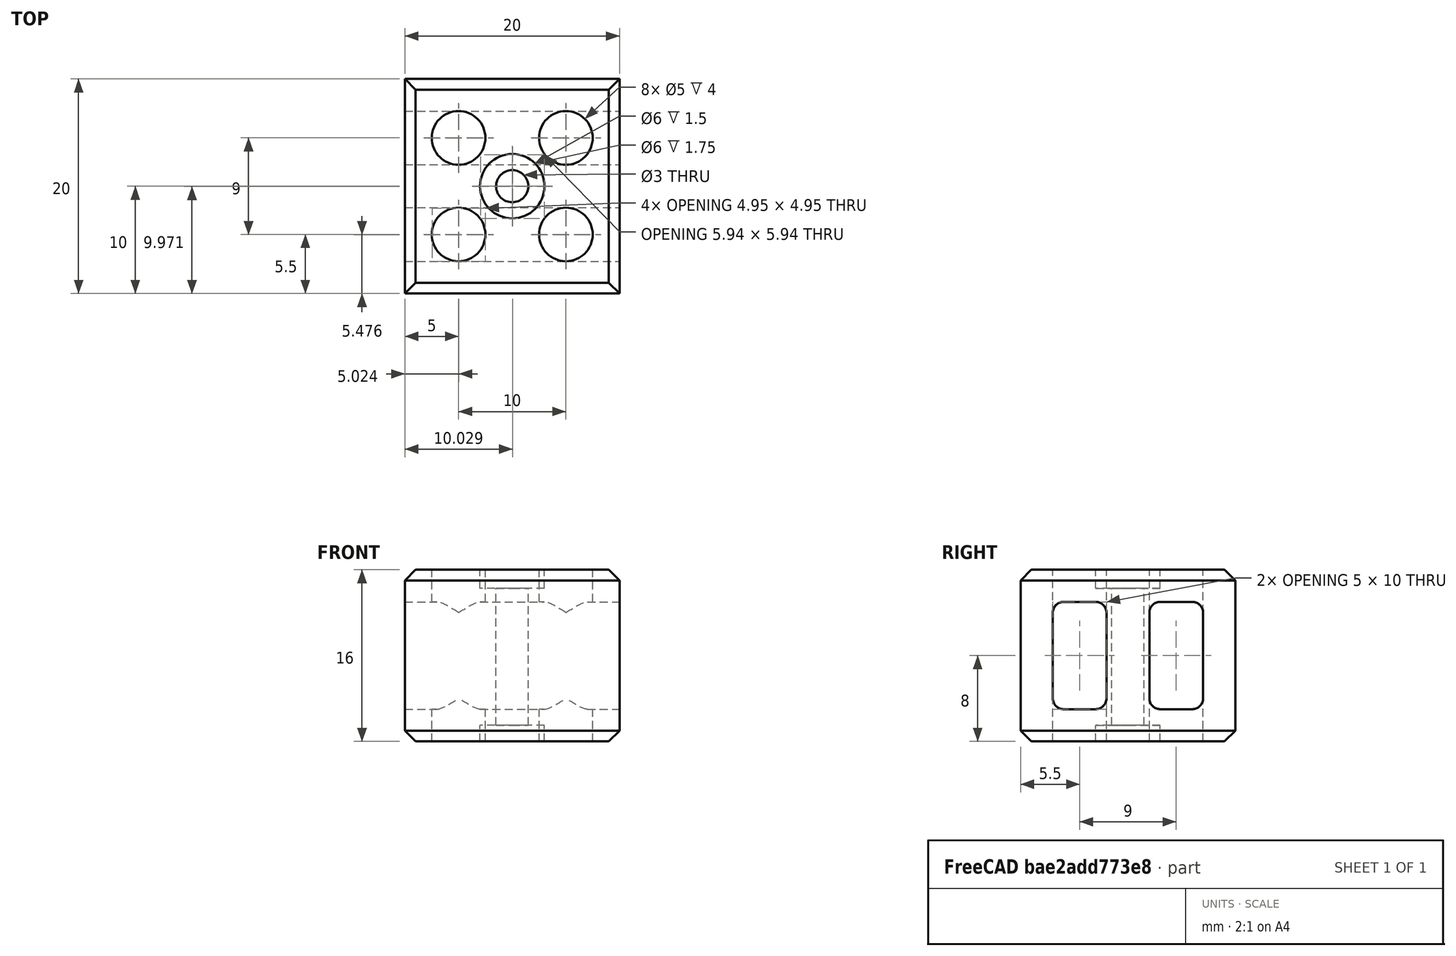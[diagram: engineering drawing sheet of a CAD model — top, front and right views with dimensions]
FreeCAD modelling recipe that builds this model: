
FCSTD DOCUMENT  (FreeCAD 0.14R3700 (Git))
Label: Cutter Ceramic Block
License: CC-BY 3.0
LicenseURL: http://creativecommons.org/licenses/by/3.0/
objects: Part::Cut×9, Part::Cylinder×7, Part::Box×3, PartDesign::Fillet×2, PartDesign::Chamfer×1
note: 22 computed .brp shape members not serialized (recipe doc carries the construction recipe); baked Part::Feature solids carry a one-line shape summary decoded from their .brp

FEATURE [Part::Box] Box  label="Cube"
  Height = 16
  Length = 20
  Width = 20
FEATURE [PartDesign::Chamfer] Chamfer
  Base = -> Box [Edge6,Edge12,Edge2,Edge10,Edge9,Edge8,Edge4,Edge11]
  Size = 1
FEATURE [Part::Box] Box001  label="Cube001"
  Height = 10
  Length = 22
  Placement = pos=(-1,12,3) rot=(0,0,1;0rad)
  Width = 5
FEATURE [Part::Box] Box002  label="Cube002"
  Height = 10
  Length = 22
  Placement = pos=(-1,3,3) rot=(0,0,1;0rad)
  Width = 5
FEATURE [Part::Cut] Cut
  Base = -> Chamfer
  Tool = -> Box002
FEATURE [Part::Cut] Cut001
  Base = -> Cut
  Tool = -> Box001
FEATURE [PartDesign::Fillet] Fillet
  Base = -> Cut001 [Edge39,Edge40,Edge38,Edge37]
  Radius = 1
FEATURE [PartDesign::Fillet] Fillet001
  Base = -> Fillet [Edge38,Edge36,Edge35,Edge33]
  Radius = 1
FEATURE [Part::Cylinder] Cylinder
  Angle = 360
  Height = 18
  Placement = pos=(5,5.5,-1) rot=(0,0,1;0rad)
  Radius = 2.5
FEATURE [Part::Cut] Cut002
  Base = -> Fillet001
  Tool = -> Cylinder
FEATURE [Part::Cylinder] Cylinder001
  Angle = 360
  Height = 18
  Placement = pos=(5,14.5,-1) rot=(0,0,1;0rad)
  Radius = 2.5
FEATURE [Part::Cylinder] Cylinder002
  Angle = 360
  Height = 18
  Placement = pos=(15,14.5,-1) rot=(0,0,1;0rad)
  Radius = 2.5
FEATURE [Part::Cylinder] Cylinder003
  Angle = 360
  Height = 18
  Placement = pos=(15,5.5,-1) rot=(0,0,1;0rad)
  Radius = 2.5
FEATURE [Part::Cut] Cut003
  Base = -> Cut002
  Tool = -> Cylinder001
FEATURE [Part::Cut] Cut004
  Base = -> Cut003
  Tool = -> Cylinder002
FEATURE [Part::Cut] Cut005
  Base = -> Cut004
  Tool = -> Cylinder003
FEATURE [Part::Cylinder] Cylinder004
  Angle = 360
  Height = 16
  Placement = pos=(10,10,0) rot=(0,0,1;0rad)
  Radius = 1.5
FEATURE [Part::Cut] Cut006
  Base = -> Cut005
  Tool = -> Cylinder004
FEATURE [Part::Cylinder] Cylinder005
  Angle = 360
  Height = 2
  Placement = pos=(10,10,-0.5) rot=(0,0,1;0rad)
  Radius = 3
FEATURE [Part::Cylinder] Cylinder006
  Angle = 360
  Height = 2
  Placement = pos=(10,10,14.25) rot=(0,0,1;0rad)
  Radius = 3
FEATURE [Part::Cut] Cut007
  Base = -> Cut006
  Tool = -> Cylinder005
FEATURE [Part::Cut] Cut008
  Base = -> Cut007
  Tool = -> Cylinder006
